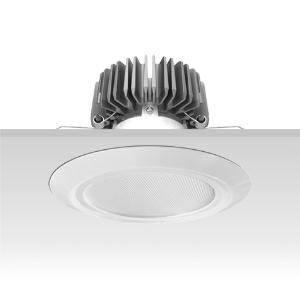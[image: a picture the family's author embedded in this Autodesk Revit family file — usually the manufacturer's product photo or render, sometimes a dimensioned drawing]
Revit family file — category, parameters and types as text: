
# Revit family: 3f_filippi_-_3f_reno_bianco_ampio_3f_filippi_-_30633_a01037_-_3f_reno_200_wh_3000-930_wide___vs_wh_dff2
name_source: partatom
category: Lighting Fixtures
units: mm (PartAtom-declared; Revit-internal decimal feet)

## family parameters
Cut with Voids When Loaded = No
Host = Face
Light Source = No
Part Type = Normal
Room Calculation Point = No
Round Connector Dimension = Use Diameter
Shared = No

## types (1)
- 3F Filippi - 3F Reno Bianco Ampio (1 x LED, 2320 lm, 37 W, 3000 K)
    Apparent Load = 37 VA
    Approval mark = CE
    CIE Flux Codes = 75 94 99 100 100
    Color Rendering = 90
    Color Temperature = 3000 K
    Control Gear = Electronic ballast
    Default Elevation = 1800 mm
    Description = ILLUMINOTECHNICAL
Luminous efficiency 100% (DLOR 100%, ULOR 0%).
Initial luminous flux of the luminaire 2320 lm.
Direct symmetric wide distribution.
Installation Interdistance Transv.D = 1.16 x hu - Long.D = 1.14 x hu.
Tabular UGR (CIE 117 - 4H-8H; S=0.25H; 70/50/20): RUG 21.5 - 21.4.
Beam angle: 74° - 74°.
Luminous efficacy 63 lm/W.
Lifetime (L90/B10): 30000 h. (tq+25°C)
Lifetime (L85/B10): 50000 h. (tq+25°C)
Lifetime (L70/B10): 80000 h. (tq+25°C)
Sudden decreased luminous flux after 50000 hours: 0% (C0).
Photobiological safety in compliance with IEC/TR 62778: RG0 risk exempt, (IEC 62471).
In compliance with IEC/EN 62722-2-1 - IEC/EN 62717 standards.

SOURCE
Compact LED module 3000/930.
Energy efficiency class (UE 2019/2020 - UE 2019/2015): E.
CIE 13.3 Colour rendering index: CRI >90 (R9 >50%).
IES TM-30 Fidelity Index: Rf = 92 Rg = 101.
CCT nominal colour temperature 3000 K.
Colour initial tolerance (MacAdam): SDCM 3.
Zhaga Book 3 compliant.

MECHANICAL
Passive heat dissipator in die-casting aluminium, oversized, for optimum thermal management of the LED module.
Parabolic element with graduated/concentric rings in white polycarbonate.
Transparent external lens with glossy and satin differentiated surfaces, with a cooling and anti-insect system in methacrylate (PMMA).
Fastening spring clips in stainless steel.
Dimensions: diameter 226 mm, height 146 mm. Weight 1.8 kg.
IP44 protection degree for exposed part, IP20 for recessed part.
Mechanical strength to impacts IK06 (1 joule).
Glow-wire test resistance 650°C.

ELECTRICAL
Wiring on a separate unit.
Halogen Free electronic wiring 230V-50/60Hz, power factor 0.95, THD <25%, constant output current, SELV, class II, 1 driver.
Power of the luminaire 37 W.
ENEC - CE.
SAFE FLICKER: PstLM=<1 and SVM=<0.4 (IEC TR 61547-1 and IEC TR 63158), to ensure a more comfortable and safe light.
Luminaire compliant with EN 60598-2-22 for power supply from a centralised emergency system CPSS (Central Power Supply System), not incorporated in the luminaire - high risk areas excluded. The default power and flux are 100% in AC and 100% in DC.
Ambient temperature from 0°C to +25°C.
Temperature class T6 max 85°C.
Relative humidity UR: <85%.

INSTALLATION
Pull-up recessed fitting.
False ceiling carving: 200 mm.
All accessories dedicated to this product are available on the Catalog and on our website www.3F-Filippi.com.

ACCESSORIES
A01037 - Anti-glare microprismatic VS moulded glass, tempered, not flammable, locked and in line with the trim, in white polycarbonate.

APPLICATIONS
Environments: architectural, commercial, exhibition areas, transit areas, corridors, shops, display windows, service areas.
In false ceilings with narrow voids.

WARNING
Luminaire designed for disposal/recycling at end-of-life.
Replaceable (LED only) light source by a professional. Replaceable control gear by a professional.
    Height = 0 mm  [stored 0 ft]
    Lamp = 1 x LED
    Lamp Light Flux = 2320 lm
    Lamp Power = 37 W
    Lamp count = 1
    Length = 226 mm
    Lifetime = 50000 h
    Luminous efficacy = 63 lm/W
    Manufacturer = 3F Filippi
    ModVariant = No
    Model = 3F Filippi - 30633+A01037 - 3F Reno 200 WH 3000-930 WIDE + VS WH
    Mounting Place = Ceiling
    Mounting Type = Recessed
    Number of Poles = 1
    OnlyDefault = Yes
    Power Factor = 1
    Product Name = 3F Filippi - 3F Reno Bianco Ampio
    Product group = recessed luminaire
    ProductGroupID = 4
    Protection Class = Protection class II
    Protection Degree = IP 20
    RLX_Detail_Level = 1
    RLX_Emergency_Light_Flux = 0 lm
    RLX_Emergency_Type = 0
    RLX_Emergency_Type_DB = No
    RlxData = <blob elided: 93645 chars, md5=45b2e895>
    Socket = socket
    Standby Power = 0 W
    System Light Flux = 2320 lm
    System Power = 37 W
    Type Comments = Product without accessories
    Type Image = 3ffilippi_3f_reno_200_wh_vs_smp.jpg
    URL = http://relux.com
    VarID = ---
    Voltage = 0 V
    Weight = 0.00 kg
    Width = 0 mm  [stored 0 ft]

note: [stored X ft] marks values corroborated as IEEE doubles in the binary element streams (Revit-internal decimal feet)

## geometry (parser evidence)
native form markers: Blend x4, Sweep x10
no freeform markers — native parametric forms only
